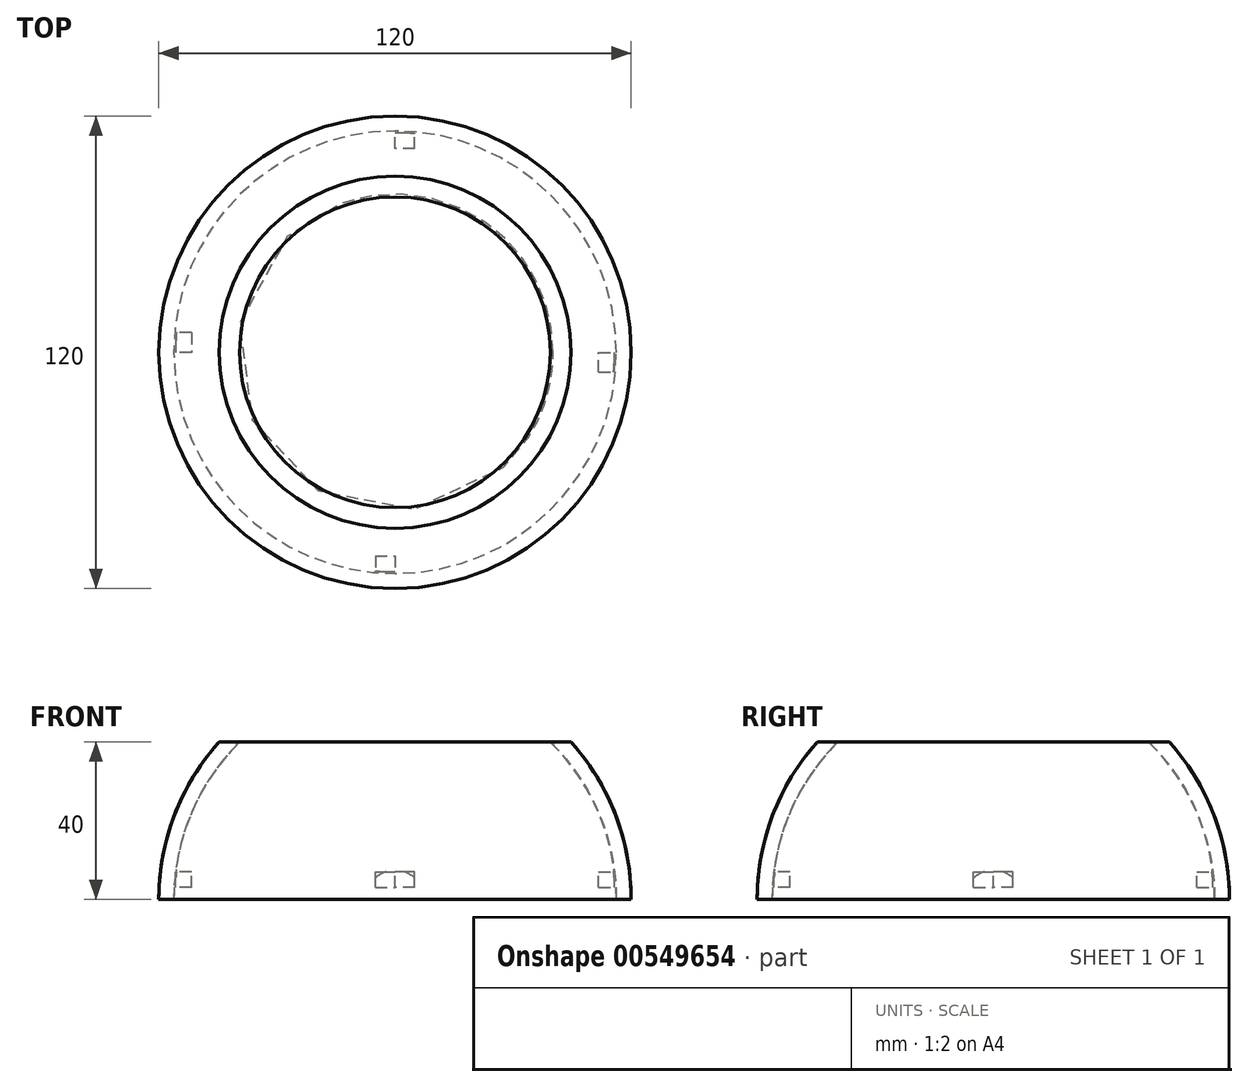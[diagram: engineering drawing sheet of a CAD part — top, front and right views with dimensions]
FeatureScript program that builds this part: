
annotation { "Feature Type Name" : "Feature", "Feature Type Description" : "" }
export const myFeature = defineFeature(function(context is Context, id is Id, definition is map)
    precondition{}
    {
        {
            var Q0;
            Q0=qCreatedBy(makeId("Front.planeOp"),FACE);
            var sketch = newSketch(context, id + "F0", { "sketchPlane" : qUnion([Q0])});
            skCircle(sketch, "E0", {"center": v(0, 0) * mm, "radius": 60 * mm, "construction": true});
            skLineSegment(sketch, "E1", {"start": v(0, 0) * mm, "end": v(-60, 0) * mm, "construction": true});
            skLineSegment(sketch, "E2", {"start": v(0, 0) * mm, "end": v(0, 60) * mm, "construction": true});
            skSolve(sketch);
        }
        {
            var Q0;
            Q0=qCreatedBy(makeId("Front.planeOp"),FACE);
            var sketch = newSketch(context, id + "F1", { "sketchPlane" : qUnion([Q0])});
            skArc(sketch, "E3", {"start": v(-44.72, 40) * mm, "mid": v(-56.05, 21.4) * mm, "end": v(-60, 0) * mm});
            skArc(sketch, "E4", {"start": v(-39.48, 40) * mm, "mid": v(-51.85, 21.68) * mm, "end": v(-56.2, 0) * mm});
            skLineSegment(sketch, "E5", {"start": v(-44.72, 40) * mm, "end": v(-39.48, 40) * mm});
            skLineSegment(sketch, "E6", {"start": v(-60, 0) * mm, "end": v(-56.2, 0) * mm});
            skLineSegment(sketch, "E7", {"start": v(0, 0) * mm, "end": v(0, 47.93) * mm, "construction": true});
            skSolve(sketch);
        }
        {
            var Q0;
            Q0 = qSketchRegion(id + "F1", true);
            var Q1;
            Q1=sQuery(id+"F1.wireOp",EDGE,"E7");
            revolve(context, id + "F2", {"entities" : qUnion([Q0]), "axis" : qUnion([Q1]), "revolveType" : RevolveType.FULL});
        }
        {
            var Q0;
            Q0=qCreatedBy(makeId("Right.planeOp"),FACE);
            var sketch = newSketch(context, id + "F3", { "sketchPlane" : qUnion([Q0])});
            skLineSegment(sketch, "E8.bottom", {"start": v(51.71, 3) * mm, "end": v(55.71, 3) * mm});
            skLineSegment(sketch, "E8.top", {"start": v(51.71, 7) * mm, "end": v(55.71, 7) * mm});
            skLineSegment(sketch, "E8.left", {"start": v(51.71, 3) * mm, "end": v(51.71, 7) * mm});
            skLineSegment(sketch, "E8.right", {"start": v(55.71, 3) * mm, "end": v(55.71, 7) * mm});
            skSolve(sketch);
        }
        {
            var Q0;
            Q0 = qSketchRegion(id + "F3", true);
            extrude(context, id + "F4", {"entities" : qUnion([Q0]), "operationType" : NewBodyOperationType.ADD, "depth" : 5 * mm, "offsetDistance" : 25 * mm});
        }
        {
            var Q0;
            Q0=makeQuery(id+"F2.opRevolve","SWEPT_BODY",BODY,{"disambiguationData":[OSD([sQuery(id+"F1.wireOp",EDGE,"E3"),sQuery(id+"F1.wireOp",EDGE,"E4"),sQuery(id+"F1.wireOp",EDGE,"E5"),sQuery(id+"F1.wireOp",EDGE,"E6")])]});
            var Q1;
            Q1=sQuery(id+"F0.wireOp",EDGE,"E2");
            circularPattern(context, id + "F5", {"entities" : qUnion([Q0]), "axis" : qUnion([Q1]), "angle" : 360 * degree, "instanceCount" : 4, "equalSpace" : true});
        }
        {
            var Q0;
            Q0=makeQuery(id+"F2.opRevolve","SWEPT_EDGE",EDGE,{"disambiguationData":[OSD([sQuery(id+"F1.wireOp",EDGE,"E4"),sQuery(id+"F1.wireOp",EDGE,"E5")])]});
            fillet(context, id + "F6", {"entities" : qUnion([Q0]), "radius" : 0.5 * mm, "tangentPropagation" : true, "allowEdgeOverflow" : false});
        }
    });
